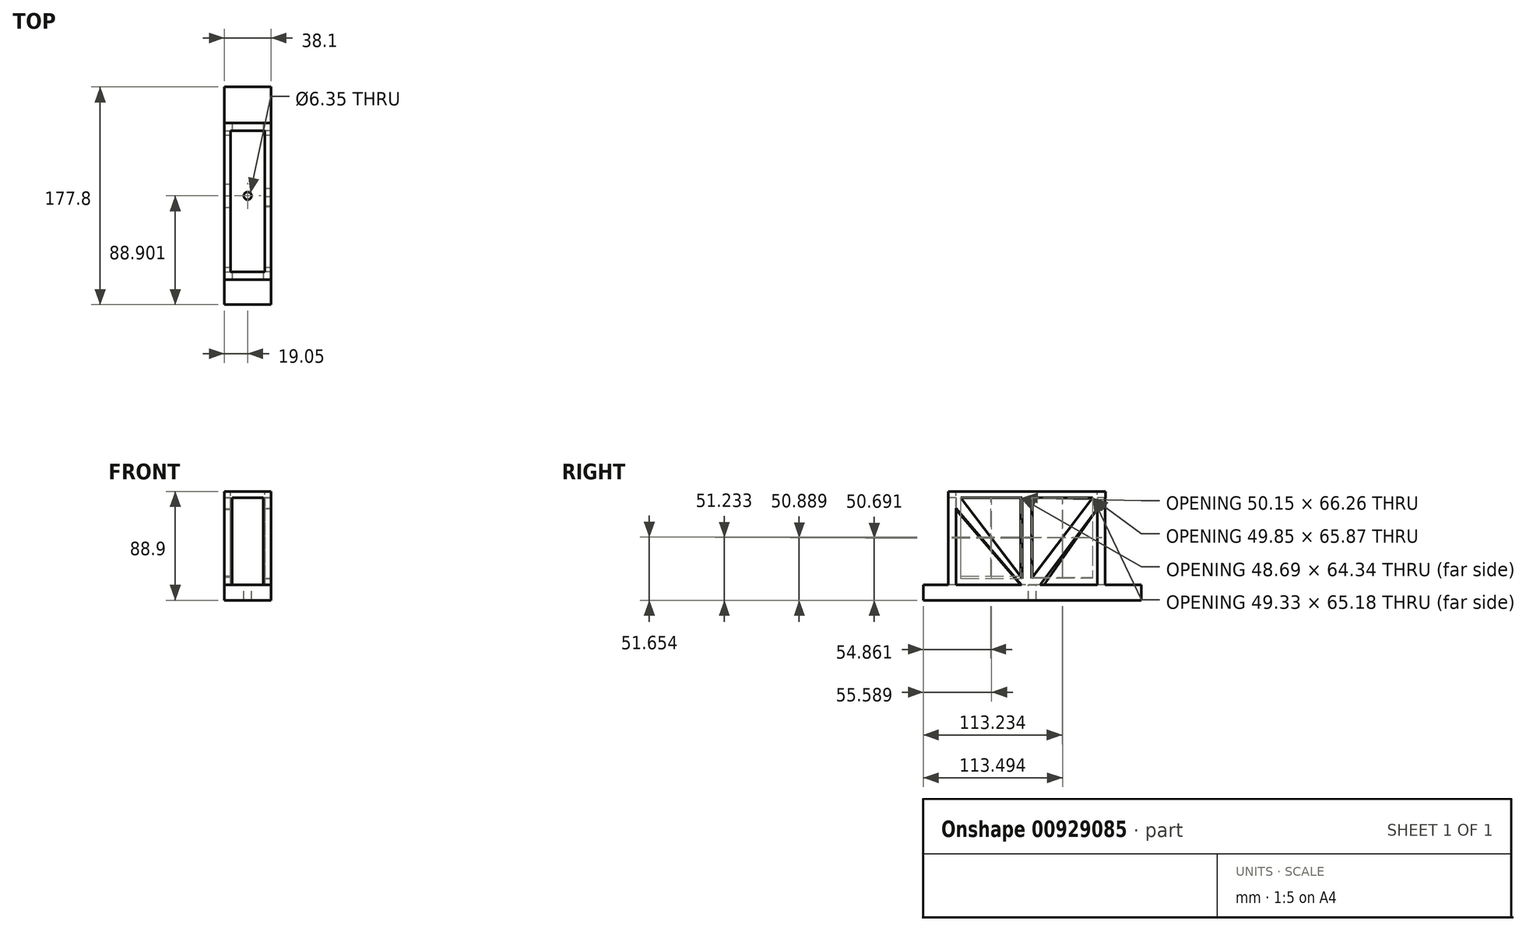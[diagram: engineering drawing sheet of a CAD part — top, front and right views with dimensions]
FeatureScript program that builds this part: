
annotation { "Feature Type Name" : "Feature", "Feature Type Description" : "" }
export const myFeature = defineFeature(function(context is Context, id is Id, definition is map)
    precondition{}
    {
        {
            var Q0;
            Q0=qCreatedBy(makeId("Right.planeOp"),FACE);
            var sketch = newSketch(context, id + "F0", { "sketchPlane" : qUnion([Q0])});
            skLineSegment(sketch, "E0.bottom", {"start": v(-87.2, -1.77) * mm, "end": v(39.8, -1.77) * mm});
            skLineSegment(sketch, "E0.top", {"start": v(-87.2, -14.47) * mm, "end": v(39.8, -14.47) * mm});
            skLineSegment(sketch, "E0.left", {"start": v(-87.2, -1.77) * mm, "end": v(-87.2, -14.47) * mm});
            skLineSegment(sketch, "E0.right", {"start": v(39.8, -1.77) * mm, "end": v(39.8, -14.47) * mm});
            skLineSegment(sketch, "E1.bottom", {"start": v(39.8, -1.77) * mm, "end": v(65.2, -1.77) * mm});
            skLineSegment(sketch, "E1.top", {"start": v(39.8, -14.47) * mm, "end": v(65.2, -14.47) * mm});
            skLineSegment(sketch, "E1.right", {"start": v(65.2, -1.77) * mm, "end": v(65.2, -14.47) * mm});
            skLineSegment(sketch, "E2.bottom", {"start": v(-87.2, -14.47) * mm, "end": v(-112.6, -14.47) * mm});
            skLineSegment(sketch, "E2.top", {"start": v(-87.2, -1.77) * mm, "end": v(-112.6, -1.77) * mm});
            skLineSegment(sketch, "E2.left", {"start": v(-87.2, -14.47) * mm, "end": v(-87.2, -1.77) * mm});
            skLineSegment(sketch, "E2.right", {"start": v(-112.6, -14.47) * mm, "end": v(-112.6, -1.77) * mm});
            skSolve(sketch);
        }
        {
            var Q0;
            Q0 = qSketchRegion(id + "F0", true);
            extrude(context, id + "F1", {"entities" : qUnion([Q0]), "depth" : 38.1 * mm, "offsetDistance" : 25.4 * mm});
        }
        {
            var Q0;
            Q0=makeQuery(id+"F1.opExtrude","SWEPT_FACE",FACE,{"disambiguationData":[OSD([sQuery(id+"F0.wireOp",EDGE,"E0.bottom"),sQuery(id+"F0.wireOp",EDGE,"E1.bottom"),sQuery(id+"F0.wireOp",EDGE,"E2.top")])]});
            var sketch = newSketch(context, id + "F2", { "sketchPlane" : qUnion([Q0])});
            skLineSegment(sketch, "E3.bottom", {"start": v(0, 35.74) * mm, "end": v(6.35, 35.74) * mm});
            skLineSegment(sketch, "E3.top", {"start": v(0, 29.4) * mm, "end": v(6.35, 29.4) * mm});
            skLineSegment(sketch, "E3.left", {"start": v(0, 35.74) * mm, "end": v(0, 29.4) * mm});
            skLineSegment(sketch, "E3.right", {"start": v(6.35, 35.74) * mm, "end": v(6.35, 29.4) * mm});
            skLineSegment(sketch, "E4.bottom", {"start": v(38.1, 35.74) * mm, "end": v(31.75, 35.74) * mm});
            skLineSegment(sketch, "E4.top", {"start": v(38.1, 29.4) * mm, "end": v(31.75, 29.4) * mm});
            skLineSegment(sketch, "E4.left", {"start": v(38.1, 35.74) * mm, "end": v(38.1, 29.4) * mm});
            skLineSegment(sketch, "E4.right", {"start": v(31.75, 35.74) * mm, "end": v(31.75, 29.4) * mm});
            skLineSegment(sketch, "E5.bottom", {"start": v(0, -85.94) * mm, "end": v(6.35, -85.94) * mm});
            skLineSegment(sketch, "E5.top", {"start": v(0, -92.29) * mm, "end": v(6.35, -92.29) * mm});
            skLineSegment(sketch, "E5.left", {"start": v(0, -85.94) * mm, "end": v(0, -92.29) * mm});
            skLineSegment(sketch, "E5.right", {"start": v(6.35, -85.94) * mm, "end": v(6.35, -92.29) * mm});
            skLineSegment(sketch, "E6.bottom", {"start": v(38.1, -85.94) * mm, "end": v(31.75, -85.94) * mm});
            skLineSegment(sketch, "E6.top", {"start": v(38.1, -92.29) * mm, "end": v(31.75, -92.29) * mm});
            skLineSegment(sketch, "E6.left", {"start": v(38.1, -85.94) * mm, "end": v(38.1, -92.29) * mm});
            skLineSegment(sketch, "E6.right", {"start": v(31.75, -85.94) * mm, "end": v(31.75, -92.29) * mm});
            skSolve(sketch);
        }
        {
            var Q0;
            Q0 = qSketchRegion(id + "F2", true);
            extrude(context, id + "F3", {"entities" : qUnion([Q0]), "operationType" : NewBodyOperationType.ADD, "depth" : 76.2 * mm, "offsetDistance" : 25.4 * mm});
        }
        {
            var Q0;
            Q0=makeQuery(id+"F3.boolean.opBoolean","MERGE",FACE,{"derivedFrom":[makeQuery(id+"F1.opExtrude","CAP_FACE",FACE,{"disambiguationData":[OSD([sQuery(id+"F0.wireOp",EDGE,"E0.bottom"),sQuery(id+"F0.wireOp",EDGE,"E0.top"),sQuery(id+"F0.wireOp",EDGE,"E1.bottom"),sQuery(id+"F0.wireOp",EDGE,"E1.top"),sQuery(id+"F0.wireOp",EDGE,"E1.right"),sQuery(id+"F0.wireOp",EDGE,"E2.bottom"),sQuery(id+"F0.wireOp",EDGE,"E2.top"),sQuery(id+"F0.wireOp",EDGE,"E2.right")])],"isStart":false}),makeQuery(id+"F3.opExtrude","SWEPT_FACE",FACE,{"disambiguationData":[OSD([sQuery(id+"F2.wireOp",EDGE,"E4.left")])]}),makeQuery(id+"F3.opExtrude","SWEPT_FACE",FACE,{"disambiguationData":[OSD([sQuery(id+"F2.wireOp",EDGE,"E6.left")])]})]});
            var sketch = newSketch(context, id + "F4", { "sketchPlane" : qUnion([Q0])});
            skLineSegment(sketch, "E7", {"start": v(35.74, 74.43) * mm, "end": v(29.4, 74.43) * mm});
            skLineSegment(sketch, "E8", {"start": v(29.4, 74.43) * mm, "end": v(-28.27, -1.77) * mm});
            skLineSegment(sketch, "E9", {"start": v(-28.27, -1.77) * mm, "end": v(-85.94, 74.43) * mm});
            skLineSegment(sketch, "E10", {"start": v(-85.94, 74.43) * mm, "end": v(-92.29, 74.43) * mm});
            skLineSegment(sketch, "E11", {"start": v(-92.29, 60.53) * mm, "end": v(-85.94, 60.53) * mm});
            skLineSegment(sketch, "E12", {"start": v(-85.94, 60.53) * mm, "end": v(-32.57, -1.77) * mm});
            skLineSegment(sketch, "E13", {"start": v(-32.57, -1.77) * mm, "end": v(-17.54, -1.77) * mm});
            skLineSegment(sketch, "E14", {"start": v(-17.54, -1.77) * mm, "end": v(29.4, 60.25) * mm});
            skPoint(sketch, "E14.endSnap0", {"position": v(29.4, 36.33) * mm});
            skLineSegment(sketch, "E15", {"start": v(29.4, 60.25) * mm, "end": v(35.74, 60.25) * mm});
            skLineSegment(sketch, "E16", {"start": v(-85.94, 74.43) * mm, "end": v(-85.94, 60.53) * mm});
            skLineSegment(sketch, "E17", {"start": v(-92.29, 74.43) * mm, "end": v(-92.29, 60.53) * mm});
            skLineSegment(sketch, "E18", {"start": v(-28.27, -1.77) * mm, "end": v(-32.57, -1.77) * mm});
            skLineSegment(sketch, "E19", {"start": v(-28.27, -1.77) * mm, "end": v(-17.54, -1.77) * mm});
            skLineSegment(sketch, "E20", {"start": v(29.4, 74.43) * mm, "end": v(29.4, 60.25) * mm});
            skLineSegment(sketch, "E21", {"start": v(35.74, 74.43) * mm, "end": v(35.74, 60.25) * mm});
            skSolve(sketch);
        }
        {
            var Q0;
            {var subQ0=sQuery(id+"F4.wireOp",EDGE,"E9");var subQ2=sQuery(id+"F4.wireOp",EDGE,"E8");Q0=qUnion([makeQuery(id+"F4.imprint","IMPRINT",FACE,{"disambiguationData":[TD([[makeQuery(id+"F4.imprint","IMPRINT",EDGE,{"derivedFrom":sQuery(id+"F4.wireOp",EDGE,"E7")}),1.0]])]}),makeQuery(id+"F4.imprint","IMPRINT",FACE,{"disambiguationData":[TD([[makeQuery(id+"F4.imprint","IMPRINT",EDGE,{"derivedFrom":sQuery(id+"F4.wireOp",EDGE,"E10")}),1.0]])]}),makeQuery(id+"F4.imprint","IMPRINT",FACE,{"disambiguationData":[TD([[makeQuery(id+"F4.imprint","IMPRINT",EDGE,{"derivedFrom":subQ2}),1.0]])]}),makeQuery(id+"F4.imprint","IMPRINT",FACE,{"disambiguationData":[TD([[makeQuery(id+"F4.imprint","IMPRINT",EDGE,{"derivedFrom":subQ0}),1.0]])]})]);}
            var Q1;
            Q1 = qSketchRegion(id + "FQBIBC5uEgxEeDU_1", true);
            extrude(context, id + "F5", {"entities" : qUnion([Q0, Q1]), "operationType" : NewBodyOperationType.ADD, "oppositeDirection" : true, "depth" : 5.08 * mm, "offsetDistance" : 25.4 * mm});
        }
        {
            var Q0;
            Q0=makeQuery(id+"F3.boolean.opBoolean","MERGE",FACE,{"derivedFrom":[makeQuery(id+"F1.opExtrude","CAP_FACE",FACE,{"disambiguationData":[OSD([sQuery(id+"F0.wireOp",EDGE,"E0.bottom"),sQuery(id+"F0.wireOp",EDGE,"E0.top"),sQuery(id+"F0.wireOp",EDGE,"E1.bottom"),sQuery(id+"F0.wireOp",EDGE,"E1.top"),sQuery(id+"F0.wireOp",EDGE,"E1.right"),sQuery(id+"F0.wireOp",EDGE,"E2.bottom"),sQuery(id+"F0.wireOp",EDGE,"E2.top"),sQuery(id+"F0.wireOp",EDGE,"E2.right")])],"isStart":true}),makeQuery(id+"F3.opExtrude","SWEPT_FACE",FACE,{"disambiguationData":[OSD([sQuery(id+"F2.wireOp",EDGE,"E3.left")])]}),makeQuery(id+"F3.opExtrude","SWEPT_FACE",FACE,{"disambiguationData":[OSD([sQuery(id+"F2.wireOp",EDGE,"E5.left")])]})]});
            var sketch = newSketch(context, id + "F6", { "sketchPlane" : qUnion([Q0])});
            skLineSegment(sketch, "E22", {"start": v(92.29, 74.43) * mm, "end": v(85.94, 74.43) * mm});
            skLineSegment(sketch, "E23", {"start": v(85.94, 74.43) * mm, "end": v(28.27, -1.77) * mm});
            skLineSegment(sketch, "E24", {"start": v(28.27, -1.77) * mm, "end": v(-29.4, 74.43) * mm});
            skLineSegment(sketch, "E25", {"start": v(-29.4, 74.43) * mm, "end": v(-35.74, 74.43) * mm});
            skLineSegment(sketch, "E26", {"start": v(-35.74, 74.43) * mm, "end": v(-35.74, 60.13) * mm});
            skLineSegment(sketch, "E27", {"start": v(-35.74, 60.13) * mm, "end": v(-29.4, 60.13) * mm});
            skLineSegment(sketch, "E28", {"start": v(-29.4, 60.13) * mm, "end": v(14.36, -1.77) * mm});
            skLineSegment(sketch, "E29", {"start": v(14.36, -1.77) * mm, "end": v(33.4, -1.77) * mm});
            skLineSegment(sketch, "E30", {"start": v(33.4, -1.77) * mm, "end": v(85.94, 59.46) * mm});
            skLineSegment(sketch, "E31", {"start": v(85.94, 59.46) * mm, "end": v(92.29, 59.46) * mm});
            skLineSegment(sketch, "E32", {"start": v(92.29, 59.46) * mm, "end": v(92.29, 74.43) * mm});
            skSolve(sketch);
        }
        {
            var Q0;
            Q0 = qSketchRegion(id + "F6", true);
            extrude(context, id + "F7", {"entities" : qUnion([Q0]), "operationType" : NewBodyOperationType.ADD, "oppositeDirection" : true, "depth" : 5.08 * mm, "offsetDistance" : 25.4 * mm});
        }
        {
            var Q0;
            Q0=makeQuery(id+"F1.opExtrude","SWEPT_FACE",FACE,{"disambiguationData":[OSD([sQuery(id+"F0.wireOp",EDGE,"E0.bottom"),sQuery(id+"F0.wireOp",EDGE,"E1.bottom"),sQuery(id+"F0.wireOp",EDGE,"E2.top")])]});
            var sketch = newSketch(context, id + "F8", { "sketchPlane" : qUnion([Q0])});
            skLineSegment(sketch, "E33", {"start": v(19.05, 65.2) * mm, "end": v(19.05, -23.7) * mm});
            skCircle(sketch, "E34", {"center": v(19.05, -23.7) * mm, "radius": 3.18 * mm});
            skSolve(sketch);
        }
        {
            var Q0;
            Q0 = qSketchRegion(id + "F8", true);
            extrude(context, id + "F9", {"entities" : qUnion([Q0]), "operationType" : NewBodyOperationType.REMOVE, "oppositeDirection" : true, "depth" : 119.63 * mm, "offsetDistance" : 25.4 * mm});
        }
        {
            var Q0;
            Q0=makeQuery(id+"F3.opExtrude","CAP_FACE",FACE,{"disambiguationData":[OSD([sQuery(id+"F2.wireOp",EDGE,"E6.bottom"),sQuery(id+"F2.wireOp",EDGE,"E6.top"),sQuery(id+"F2.wireOp",EDGE,"E6.left"),sQuery(id+"F2.wireOp",EDGE,"E6.right")])],"isStart":false});
            var sketch = newSketch(context, id + "F10", { "sketchPlane" : qUnion([Q0])});
            skLineSegment(sketch, "E35.bottom", {"start": v(31.75, -92.29) * mm, "end": v(0, -92.29) * mm});
            skLineSegment(sketch, "E35.top", {"start": v(31.75, -85.94) * mm, "end": v(0, -85.94) * mm});
            skLineSegment(sketch, "E35.left", {"start": v(31.75, -92.29) * mm, "end": v(31.75, -85.94) * mm});
            skLineSegment(sketch, "E35.right", {"start": v(0, -92.29) * mm, "end": v(0, -85.94) * mm});
            skSolve(sketch);
        }
        {
            var Q0;
            Q0 = qSketchRegion(id + "F10", true);
            extrude(context, id + "F11", {"entities" : qUnion([Q0]), "operationType" : NewBodyOperationType.ADD, "oppositeDirection" : true, "depth" : 5.08 * mm, "offsetDistance" : 25.4 * mm});
        }
        {
            var Q0;
            Q0=makeQuery(id+"F3.opExtrude","CAP_FACE",FACE,{"disambiguationData":[OSD([sQuery(id+"F2.wireOp",EDGE,"E4.bottom"),sQuery(id+"F2.wireOp",EDGE,"E4.top"),sQuery(id+"F2.wireOp",EDGE,"E4.left"),sQuery(id+"F2.wireOp",EDGE,"E4.right")])],"isStart":false});
            var sketch = newSketch(context, id + "F12", { "sketchPlane" : qUnion([Q0])});
            skLineSegment(sketch, "E36.bottom", {"start": v(0, 35.83) * mm, "end": v(38.1, 35.83) * mm});
            skLineSegment(sketch, "E36.top", {"start": v(0, 29.4) * mm, "end": v(38.1, 29.4) * mm});
            skLineSegment(sketch, "E36.left", {"start": v(0, 35.83) * mm, "end": v(0, 29.4) * mm});
            skLineSegment(sketch, "E36.right", {"start": v(38.1, 35.83) * mm, "end": v(38.1, 29.4) * mm});
            skSolve(sketch);
        }
        {
            var Q0;
            Q0 = qSketchRegion(id + "F12", true);
            extrude(context, id + "F13", {"entities" : qUnion([Q0]), "operationType" : NewBodyOperationType.ADD, "oppositeDirection" : true, "depth" : 5.08 * mm, "offsetDistance" : 25.4 * mm});
        }
        {
            var Q0;
            Q0=makeQuery(id+"F13.boolean.opBoolean","MERGE",FACE,{"derivedFrom":[makeQuery(id+"F3.opExtrude","CAP_FACE",FACE,{"disambiguationData":[OSD([sQuery(id+"F2.wireOp",EDGE,"E4.bottom"),sQuery(id+"F2.wireOp",EDGE,"E4.top"),sQuery(id+"F2.wireOp",EDGE,"E4.left"),sQuery(id+"F2.wireOp",EDGE,"E4.right")])],"isStart":false}),makeQuery(id+"F3.opExtrude","CAP_FACE",FACE,{"disambiguationData":[OSD([sQuery(id+"F2.wireOp",EDGE,"E3.bottom"),sQuery(id+"F2.wireOp",EDGE,"E3.top"),sQuery(id+"F2.wireOp",EDGE,"E3.left"),sQuery(id+"F2.wireOp",EDGE,"E3.right")])],"isStart":false}),makeQuery(id+"F13.opExtrude","CAP_FACE",FACE,{"disambiguationData":[OSD([sQuery(id+"F12.wireOp",EDGE,"E36.bottom"),sQuery(id+"F12.wireOp",EDGE,"E36.top"),sQuery(id+"F12.wireOp",EDGE,"E36.left"),sQuery(id+"F12.wireOp",EDGE,"E36.right")])],"isStart":true})]});
            var sketch = newSketch(context, id + "F14", { "sketchPlane" : qUnion([Q0])});
            skLineSegment(sketch, "E37.bottom", {"start": v(0, 35.83) * mm, "end": v(5.08, 35.83) * mm});
            skLineSegment(sketch, "E37.top", {"start": v(0, -92.24) * mm, "end": v(5.08, -92.24) * mm});
            skLineSegment(sketch, "E37.left", {"start": v(0, 35.83) * mm, "end": v(0, -92.24) * mm});
            skLineSegment(sketch, "E37.right", {"start": v(5.08, 35.83) * mm, "end": v(5.08, -92.24) * mm});
            skSolve(sketch);
        }
        {
            var Q0;
            Q0 = qSketchRegion(id + "F14", true);
            extrude(context, id + "F15", {"entities" : qUnion([Q0]), "operationType" : NewBodyOperationType.ADD, "oppositeDirection" : true, "depth" : 5.08 * mm, "offsetDistance" : 25.4 * mm});
        }
        {
            var Q0;
            Q0=makeQuery(id+"F15.boolean.opBoolean","MERGE",FACE,{"derivedFrom":[makeQuery(id+"F11.boolean.opBoolean","MERGE",FACE,{"derivedFrom":[makeQuery(id+"F3.opExtrude","CAP_FACE",FACE,{"disambiguationData":[OSD([sQuery(id+"F2.wireOp",EDGE,"E6.bottom"),sQuery(id+"F2.wireOp",EDGE,"E6.top"),sQuery(id+"F2.wireOp",EDGE,"E6.left"),sQuery(id+"F2.wireOp",EDGE,"E6.right")])],"isStart":false}),makeQuery(id+"F3.opExtrude","CAP_FACE",FACE,{"disambiguationData":[OSD([sQuery(id+"F2.wireOp",EDGE,"E5.bottom"),sQuery(id+"F2.wireOp",EDGE,"E5.top"),sQuery(id+"F2.wireOp",EDGE,"E5.left"),sQuery(id+"F2.wireOp",EDGE,"E5.right")])],"isStart":false}),makeQuery(id+"F11.opExtrude","CAP_FACE",FACE,{"disambiguationData":[OSD([sQuery(id+"F10.wireOp",EDGE,"E35.bottom"),sQuery(id+"F10.wireOp",EDGE,"E35.top"),sQuery(id+"F10.wireOp",EDGE,"E35.left"),sQuery(id+"F10.wireOp",EDGE,"E35.right")])],"isStart":true})]}),makeQuery(id+"F13.boolean.opBoolean","MERGE",FACE,{"derivedFrom":[makeQuery(id+"F3.opExtrude","CAP_FACE",FACE,{"disambiguationData":[OSD([sQuery(id+"F2.wireOp",EDGE,"E4.bottom"),sQuery(id+"F2.wireOp",EDGE,"E4.top"),sQuery(id+"F2.wireOp",EDGE,"E4.left"),sQuery(id+"F2.wireOp",EDGE,"E4.right")])],"isStart":false}),makeQuery(id+"F3.opExtrude","CAP_FACE",FACE,{"disambiguationData":[OSD([sQuery(id+"F2.wireOp",EDGE,"E3.bottom"),sQuery(id+"F2.wireOp",EDGE,"E3.top"),sQuery(id+"F2.wireOp",EDGE,"E3.left"),sQuery(id+"F2.wireOp",EDGE,"E3.right")])],"isStart":false}),makeQuery(id+"F13.opExtrude","CAP_FACE",FACE,{"disambiguationData":[OSD([sQuery(id+"F12.wireOp",EDGE,"E36.bottom"),sQuery(id+"F12.wireOp",EDGE,"E36.top"),sQuery(id+"F12.wireOp",EDGE,"E36.left"),sQuery(id+"F12.wireOp",EDGE,"E36.right")])],"isStart":true})]}),makeQuery(id+"F15.opExtrude","CAP_FACE",FACE,{"disambiguationData":[OSD([sQuery(id+"F14.wireOp",EDGE,"E37.bottom"),sQuery(id+"F14.wireOp",EDGE,"E37.top"),sQuery(id+"F14.wireOp",EDGE,"E37.left"),sQuery(id+"F14.wireOp",EDGE,"E37.right")])],"isStart":true})]});
            var sketch = newSketch(context, id + "F16", { "sketchPlane" : qUnion([Q0])});
            skLineSegment(sketch, "E38.bottom", {"start": v(38.1, 35.83) * mm, "end": v(33.02, 35.83) * mm});
            skLineSegment(sketch, "E38.top", {"start": v(38.1, -92.29) * mm, "end": v(33.02, -92.29) * mm});
            skLineSegment(sketch, "E38.left", {"start": v(38.1, 35.83) * mm, "end": v(38.1, -92.29) * mm});
            skLineSegment(sketch, "E38.right", {"start": v(33.02, 35.83) * mm, "end": v(33.02, -92.29) * mm});
            skSolve(sketch);
        }
        {
            var Q0;
            Q0 = qSketchRegion(id + "F16", true);
            extrude(context, id + "F17", {"entities" : qUnion([Q0]), "operationType" : NewBodyOperationType.ADD, "oppositeDirection" : true, "depth" : 5.08 * mm, "offsetDistance" : 25.4 * mm});
        }
        {
            var Q0;
            {var subQ0=sQuery(id+"F4.wireOp",EDGE,"E13");Q0=makeQuery(id+"F17.boolean.opBoolean","MERGE",FACE,{"derivedFrom":[makeQuery(id+"F13.boolean.opBoolean","MERGE",FACE,{"derivedFrom":[makeQuery(id+"F5.boolean.opBoolean","MERGE",FACE,{"derivedFrom":[makeQuery(id+"F3.boolean.opBoolean","MERGE",FACE,{"derivedFrom":[makeQuery(id+"F1.opExtrude","CAP_FACE",FACE,{"disambiguationData":[OSD([sQuery(id+"F0.wireOp",EDGE,"E0.bottom"),sQuery(id+"F0.wireOp",EDGE,"E0.top"),sQuery(id+"F0.wireOp",EDGE,"E1.bottom"),sQuery(id+"F0.wireOp",EDGE,"E1.top"),sQuery(id+"F0.wireOp",EDGE,"E1.right"),sQuery(id+"F0.wireOp",EDGE,"E2.bottom"),sQuery(id+"F0.wireOp",EDGE,"E2.top"),sQuery(id+"F0.wireOp",EDGE,"E2.right")])],"isStart":false}),makeQuery(id+"F3.opExtrude","SWEPT_FACE",FACE,{"disambiguationData":[OSD([sQuery(id+"F2.wireOp",EDGE,"E4.left")])]}),makeQuery(id+"F3.opExtrude","SWEPT_FACE",FACE,{"disambiguationData":[OSD([sQuery(id+"F2.wireOp",EDGE,"E6.left")])]})]}),makeQuery(id+"F5.opExtrude","CAP_FACE",FACE,{"disambiguationData":[OSD([sQuery(id+"F4.wireOp",EDGE,"E7"),sQuery(id+"F4.wireOp",EDGE,"E8"),subQ0,sQuery(id+"F4.wireOp",EDGE,"E14"),sQuery(id+"F4.wireOp",EDGE,"E15"),sQuery(id+"F4.wireOp",EDGE,"E21")])],"isStart":true}),makeQuery(id+"F5.opExtrude","CAP_FACE",FACE,{"disambiguationData":[OSD([sQuery(id+"F4.wireOp",EDGE,"E9"),sQuery(id+"F4.wireOp",EDGE,"E10"),sQuery(id+"F4.wireOp",EDGE,"E11"),sQuery(id+"F4.wireOp",EDGE,"E12"),subQ0,sQuery(id+"F4.wireOp",EDGE,"E17")])],"isStart":true})]}),makeQuery(id+"F13.opExtrude","SWEPT_FACE",FACE,{"disambiguationData":[OSD([sQuery(id+"F12.wireOp",EDGE,"E36.right")])]})]}),makeQuery(id+"F17.opExtrude","SWEPT_FACE",FACE,{"disambiguationData":[OSD([sQuery(id+"F16.wireOp",EDGE,"E38.left")])]})]});}
            var sketch = newSketch(context, id + "F18", { "sketchPlane" : qUnion([Q0])});
            skLineSegment(sketch, "E39.bottom", {"start": v(-31.95, 69.35) * mm, "end": v(-24.3, 69.35) * mm});
            skLineSegment(sketch, "E39.top", {"start": v(-31.95, -1.77) * mm, "end": v(-24.3, -1.77) * mm});
            skLineSegment(sketch, "E39.left", {"start": v(-31.95, 69.35) * mm, "end": v(-31.95, -1.77) * mm});
            skLineSegment(sketch, "E39.right", {"start": v(-24.3, 69.35) * mm, "end": v(-24.3, -1.77) * mm});
            skSolve(sketch);
        }
        {
            var Q0;
            Q0 = qSketchRegion(id + "F18", true);
            extrude(context, id + "F19", {"entities" : qUnion([Q0]), "operationType" : NewBodyOperationType.ADD, "oppositeDirection" : true, "depth" : 5.08 * mm, "offsetDistance" : 25.4 * mm});
        }
        {
            var Q0;
            {var subQ0=sQuery(id+"F6.wireOp",EDGE,"E29");Q0=makeQuery(id+"F15.boolean.opBoolean","MERGE",FACE,{"derivedFrom":[makeQuery(id+"F13.boolean.opBoolean","MERGE",FACE,{"derivedFrom":[makeQuery(id+"F7.boolean.opBoolean","MERGE",FACE,{"derivedFrom":[makeQuery(id+"F3.boolean.opBoolean","MERGE",FACE,{"derivedFrom":[makeQuery(id+"F1.opExtrude","CAP_FACE",FACE,{"disambiguationData":[OSD([sQuery(id+"F0.wireOp",EDGE,"E0.bottom"),sQuery(id+"F0.wireOp",EDGE,"E0.top"),sQuery(id+"F0.wireOp",EDGE,"E1.bottom"),sQuery(id+"F0.wireOp",EDGE,"E1.top"),sQuery(id+"F0.wireOp",EDGE,"E1.right"),sQuery(id+"F0.wireOp",EDGE,"E2.bottom"),sQuery(id+"F0.wireOp",EDGE,"E2.top"),sQuery(id+"F0.wireOp",EDGE,"E2.right")])],"isStart":true}),makeQuery(id+"F3.opExtrude","SWEPT_FACE",FACE,{"disambiguationData":[OSD([sQuery(id+"F2.wireOp",EDGE,"E3.left")])]}),makeQuery(id+"F3.opExtrude","SWEPT_FACE",FACE,{"disambiguationData":[OSD([sQuery(id+"F2.wireOp",EDGE,"E5.left")])]})]}),makeQuery(id+"F7.opExtrude","CAP_FACE",FACE,{"disambiguationData":[OSD([sQuery(id+"F6.wireOp",EDGE,"E22"),sQuery(id+"F6.wireOp",EDGE,"E23"),subQ0,sQuery(id+"F6.wireOp",EDGE,"E30"),sQuery(id+"F6.wireOp",EDGE,"E31"),sQuery(id+"F6.wireOp",EDGE,"E32")])],"isStart":true}),makeQuery(id+"F7.opExtrude","CAP_FACE",FACE,{"disambiguationData":[OSD([sQuery(id+"F6.wireOp",EDGE,"E24"),sQuery(id+"F6.wireOp",EDGE,"E25"),sQuery(id+"F6.wireOp",EDGE,"E26"),sQuery(id+"F6.wireOp",EDGE,"E27"),sQuery(id+"F6.wireOp",EDGE,"E28"),subQ0])],"isStart":true})]}),makeQuery(id+"F13.opExtrude","SWEPT_FACE",FACE,{"disambiguationData":[OSD([sQuery(id+"F12.wireOp",EDGE,"E36.left")])]})]}),makeQuery(id+"F15.opExtrude","SWEPT_FACE",FACE,{"disambiguationData":[OSD([sQuery(id+"F14.wireOp",EDGE,"E37.left")])]})]});}
            var sketch = newSketch(context, id + "F20", { "sketchPlane" : qUnion([Q0])});
            skLineSegment(sketch, "E40.bottom", {"start": v(23.78, 69.35) * mm, "end": v(33.4, 69.35) * mm});
            skLineSegment(sketch, "E40.top", {"start": v(23.78, -3.9) * mm, "end": v(33.4, -3.9) * mm});
            skLineSegment(sketch, "E40.left", {"start": v(23.78, 69.35) * mm, "end": v(23.78, -3.9) * mm});
            skLineSegment(sketch, "E40.right", {"start": v(33.4, 69.35) * mm, "end": v(33.4, -3.9) * mm});
            skSolve(sketch);
        }
        {
            var Q0;
            Q0 = qSketchRegion(id + "F20", true);
            extrude(context, id + "F21", {"entities" : qUnion([Q0]), "operationType" : NewBodyOperationType.ADD, "oppositeDirection" : true, "depth" : 5.08 * mm, "offsetDistance" : 25.4 * mm});
        }
    });
